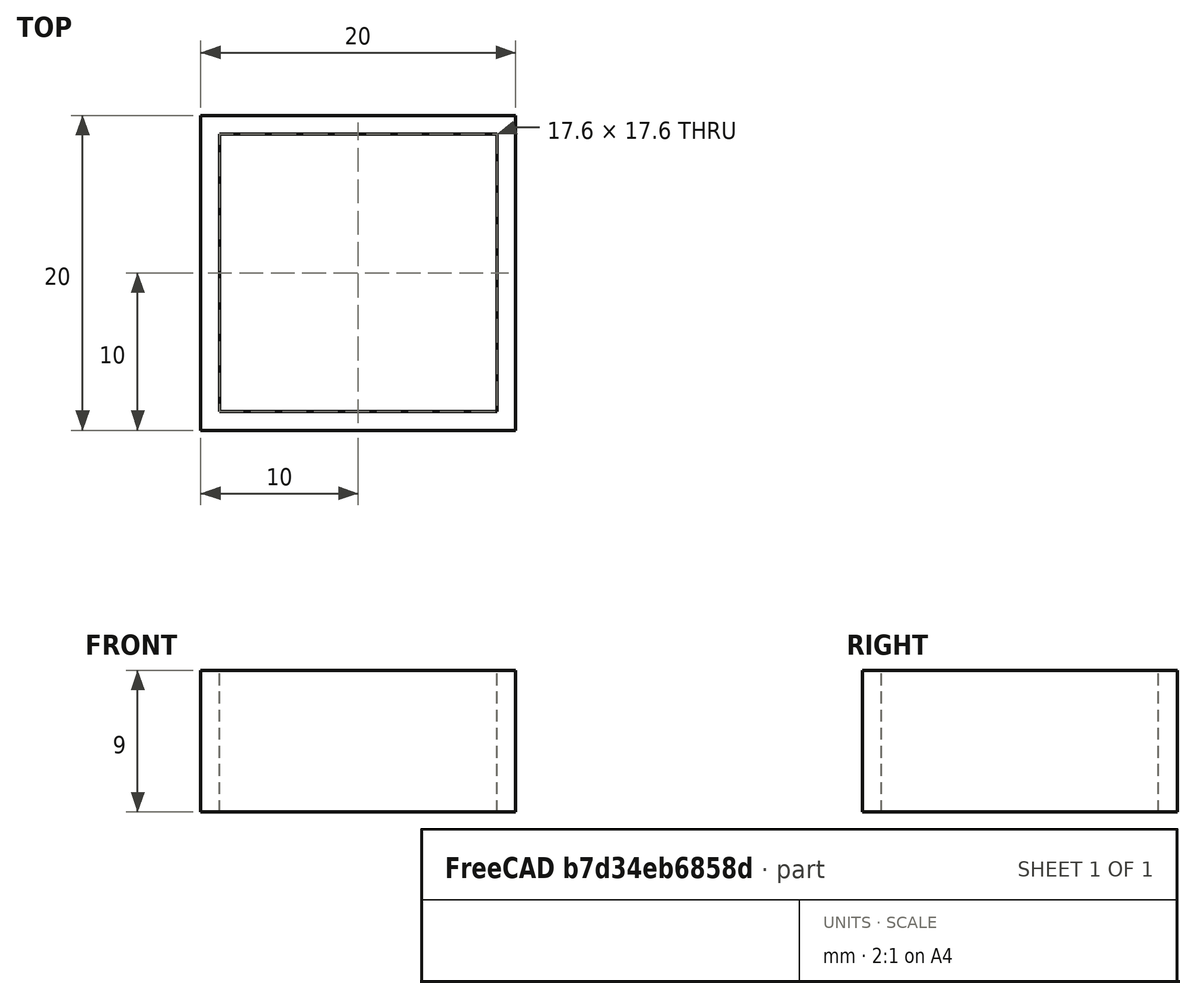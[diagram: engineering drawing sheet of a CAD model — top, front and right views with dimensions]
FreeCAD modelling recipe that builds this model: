
FCSTD DOCUMENT  (FreeCAD 0.19R24366 (Git))
Label: test
License: All rights reserved
LicenseURL: http://en.wikipedia.org/wiki/All_rights_reserved
objects: Spreadsheet::Sheet×1, Sketcher::SketchObject×1, PartDesign::Pad×1, PartDesign::Body×1, App::Part×1, Mesh::Feature×1
note: 4 computed .brp shape members not serialized (recipe doc carries the construction recipe); baked Part::Feature solids carry a one-line shape summary decoded from their .brp

FEATURE [Spreadsheet::Sheet] Spreadsheet
  cells = A1=cube_length; B1(cube_length)==20mm; A2=cube_height; B2(cube_height)==layer_width * 15; C2=15 x layer_width; A3=layer_width; B3(layer_width)==0.6mm; A4=layer_height; B4(layer_height)==0.3mm; A5=cube_walls; B5(cube_walls)=2
FEATURE [Sketcher::SketchObject] Sketch
  FullyConstrained = true
  MapMode = 5
  Support = -> [XY_Plane001]
  expr: Constraints[6] = Spreadsheet.cube_length
  expr: Constraints[7] = Spreadsheet.cube_length
  expr: Constraints[18] = Spreadsheet.cube_length - Spreadsheet.layer_width * 2 * Spreadsheet.cube_walls
  expr: Constraints[19] = Spreadsheet.cube_length - Spreadsheet.layer_width * 2 * Spreadsheet.cube_walls
  sketch-geometry (8):
    g0: LineSegment StartX=-10 StartY=10 StartZ=0 EndX=10 EndY=10 EndZ=0
    g1: LineSegment StartX=10 StartY=10 StartZ=0 EndX=10 EndY=-10 EndZ=0
    g2: LineSegment StartX=10 StartY=-10 StartZ=0 EndX=-10 EndY=-10 EndZ=0
    g3: LineSegment StartX=-10 StartY=-10 StartZ=0 EndX=-10 EndY=10 EndZ=0
    g4: LineSegment StartX=-8.8 StartY=8.8 StartZ=0 EndX=8.8 EndY=8.8 EndZ=0
    g5: LineSegment StartX=8.8 StartY=8.8 StartZ=0 EndX=8.8 EndY=-8.8 EndZ=0
    g6: LineSegment StartX=8.8 StartY=-8.8 StartZ=0 EndX=-8.8 EndY=-8.8 EndZ=0
    g7: LineSegment StartX=-8.8 StartY=-8.8 StartZ=0 EndX=-8.8 EndY=8.8 EndZ=0
  constraints (20):
    c: Coincident(g0,g1)
    c: Coincident(g1,g2)
    c: Coincident(g2,g3)
    c: Coincident(g3,g0)
    c: Horizontal(g2)
    c: Vertical(g3)
    c: DistanceX(g0,g0) = 20
    c: DistanceY(g1,g0) = 20
    c: Symmetric(g0,g0,g-2)
    c: Symmetric(g0,g1,g-1)
    c: Coincident(g4,g5)
    c: Coincident(g5,g6)
    c: Coincident(g6,g7)
    c: Coincident(g7,g4)
    c: Horizontal(g6)
    c: Vertical(g7)
    c: Symmetric(g4,g5,g-1)
    c: Symmetric(g4,g4,g-2)
    c: DistanceX(g4,g4) = 17.6
    c: DistanceY(g5,g4) = 17.6
FEATURE [PartDesign::Pad] Pad
  Direction = (1,1,1)
  Length = 9
  Length2 = 100
  Profile = -> Sketch
  Type = 0
  expr: Length = Spreadsheet.cube_height
FEATURE [PartDesign::Body] Body  label="TestCube"
  Group = -> [Sketch,Pad]
  Origin = -> Origin001
  Tip = -> Pad
FEATURE [App::Part] Part  label="Flow Test"
  Group = -> [Body]
  Origin = -> Origin
FEATURE [Mesh::Feature] Mesh  label="TestCube-0.6-nozzle"
